# Revit family: KEUCO_14985010000
name_source: partatom
category: Allgemeines Modell
revit_build: Autodesk Revit 2016 (Build: 20150220_1215(x64)
units: mm (PartAtom-declared; Revit-internal decimal feet)

## family parameters
Arbeitsebenenbasiert = Ja
Beim Laden mit Abzugskörper schneiden = Nein
Bemaßung runder Anschluss = Durchmesser verwenden
Gemeinsam genutzt = Nein
Immer vertikal = Nein
Kann Basisbauteil für Bewehrung sein = Nein
Raumberechnungspunkt = Nein
Teiletyp = Normal

## types (3) — shared parameters
Beschreibung = --
Gewicht = 2.718
Hersteller = KEUCO
Kategorie = ACC
Material Oben = Schwarzgrau (RAL 7021)
Rail Length = 851 mm  [stored 2.79199 ft]
Serie = Plan
URL = https://www.keuco.com
Verwendung = WP
Vorgabe-Ansicht = 1219 mm

## per-type parameters (varying)
| type | Artikelnummer | Ausschreibungstext | Stange Material |
| 14985010000 | 14985010000
14985010000 | KEUCO PLAN Papiertuchspender 14985010000
Hochglanzverchromter Papiertuchhalter zur Wandmontage 
für gefalzte Papierhandtücher 
mit einer Länge zwischen 240 - 254 mm und
einer Breite von 100 - 120 mm
Höhe 372 mm, Breite 320 mm, Ausladung 140 mm
Der Papiertuchhalter wird verdeckt angebracht
Lieferung inkl. korrosionsfreiem Befestigungsmaterial | Verchromt |
| 14985070000 | 14985070000 | KEUCO PLAN Papiertuchspender 14985070000
Papiertuchhalter aus hochwertigem Edelstahl-finish 
zur Wandmontage, für gefalzte Papierhandtücher 
mit einer Länge zwischen 240 - 254 mm und
einer Breite von 100 - 120 mm
Höhe 372 mm, Breite 320 mm, Ausladung 140 mm
Der Papiertuchhalter wird verdeckt angebracht
Lieferung inkl. korrosionsfreiem Befestigungsmaterial | Edelstahl |
| 14985170000 | 14985170000
14985170000 | KEUCO PLAN Papiertuchspender 14985170000
Papiertuchspender aus silber-eloxiertem Aluminium 
zur Wandmontage, für gefalzte Papierhandtücher 
mit einer Länge zwischen 240 - 254 mm und
einer Breite von 100 - 120 mm
Höhe 372 mm, Breite 320 mm, Ausladung 140 mm
Der Papiertuchhalter wird verdeckt angebracht
Lieferung inkl. korrosionsfreiem Befestigungsmaterial | Aluminium silber-eloxiert (E6 EV1) |

note: [stored X ft] marks values corroborated as IEEE doubles in the binary element streams (Revit-internal decimal feet)

## geometry (parser evidence)
native form markers: Sweep x3
no freeform markers — native parametric forms only
